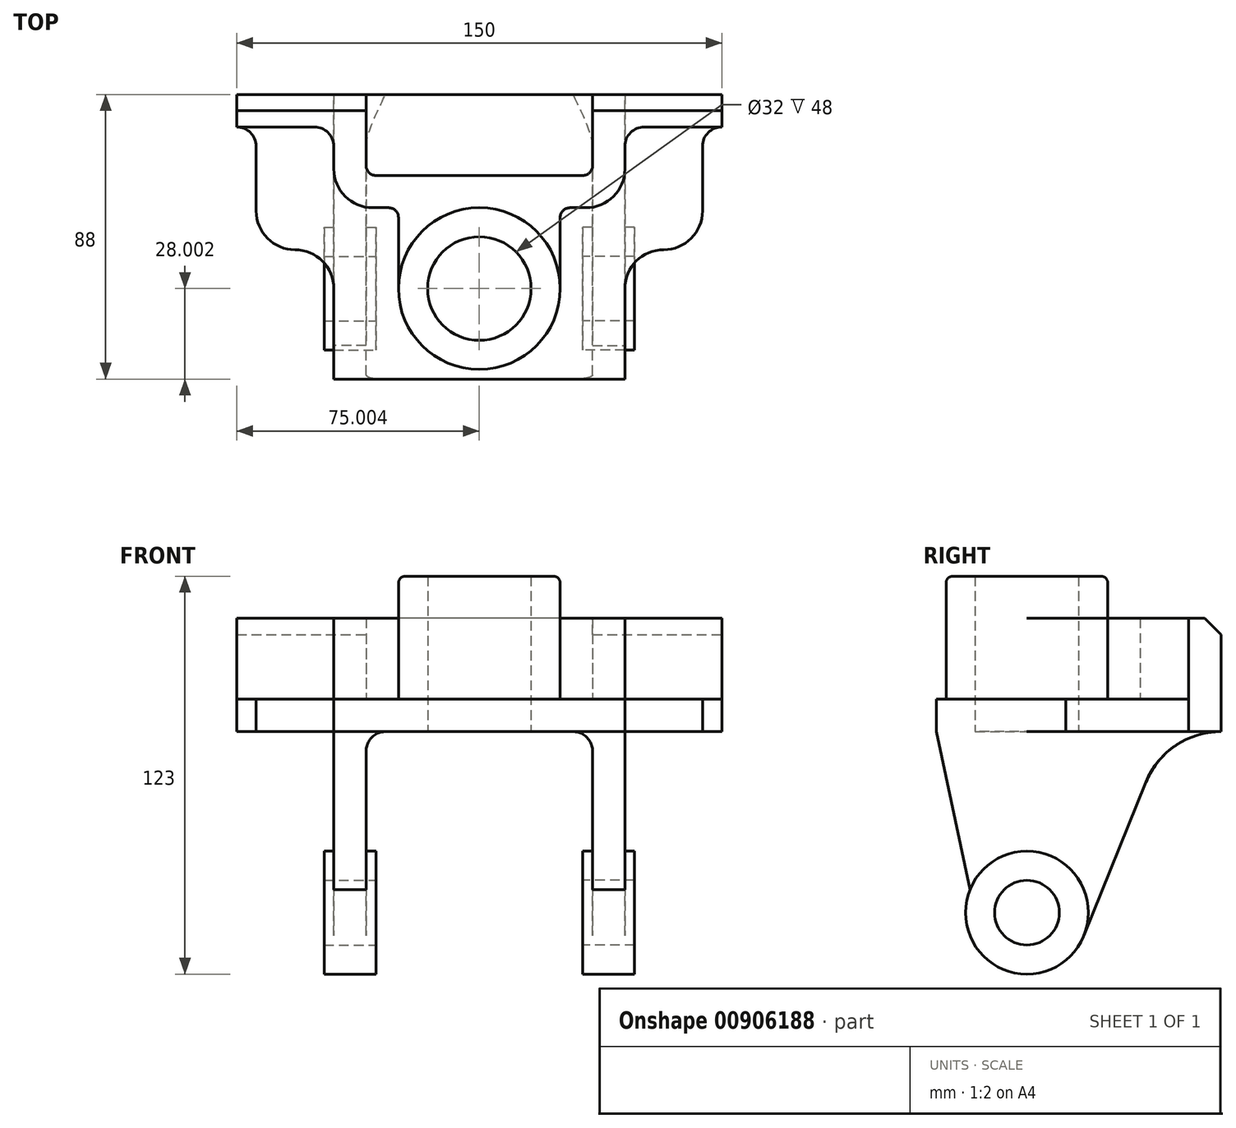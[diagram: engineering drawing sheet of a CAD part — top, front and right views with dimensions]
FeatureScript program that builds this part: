
annotation { "Feature Type Name" : "Feature", "Feature Type Description" : "" }
export const myFeature = defineFeature(function(context is Context, id is Id, definition is map)
    precondition{}
    {
        {
            var Q0;
            Q0=qCreatedBy(makeId("Top.planeOp"),FACE);
            var sketch = newSketch(context, id + "F0", { "sketchPlane" : qUnion([Q0])});
            skLineSegment(sketch, "E0.top", {"start": v(-82.05, 47.38) * mm, "end": v(67.95, 47.38) * mm});
            skLineSegment(sketch, "E0.left", {"start": v(-82.05, 37.38) * mm, "end": v(-82.05, 47.38) * mm});
            skLineSegment(sketch, "E0.right", {"start": v(67.95, 37.38) * mm, "end": v(67.95, 47.38) * mm});
            skLineSegment(sketch, "E1.0", {"start": v(61.95, 11.38) * mm, "end": v(61.95, 31.38) * mm});
            skLineSegment(sketch, "E2.0", {"start": v(-76.05, 11.38) * mm, "end": v(-76.05, 31.38) * mm});
            skArc(sketch, "E3.filletArc", {"start": v(67.95, 37.38) * mm, "mid": v(63.71, 35.62) * mm, "end": v(61.95, 31.38) * mm});
            skArc(sketch, "E4.filletArc", {"start": v(-76.05, 31.38) * mm, "mid": v(-77.8, 35.62) * mm, "end": v(-82.05, 37.38) * mm});
            skLineSegment(sketch, "E5.0", {"start": v(37.95, -12.62) * mm, "end": v(37.95, -40.62) * mm});
            skLineSegment(sketch, "E6.0", {"start": v(49.95, -0.62) * mm, "end": v(49.95, -0.62) * mm});
            skArc(sketch, "E7.filletArc", {"start": v(49.95, -0.62) * mm, "mid": v(41.47, -4.13) * mm, "end": v(37.95, -12.62) * mm});
            skArc(sketch, "E8.filletArc", {"start": v(49.95, -0.62) * mm, "mid": v(58.44, 2.9) * mm, "end": v(61.95, 11.38) * mm});
            skLineSegment(sketch, "E9", {"start": v(-7.05, 47.38) * mm, "end": v(-7.05, -47.77) * mm, "construction": true});
            skArc(sketch, "E10.MirrorCS", {"start": v(-64.05, -0.62) * mm, "mid": v(-72.53, 2.9) * mm, "end": v(-76.05, 11.38) * mm});
            skArc(sketch, "E11.MirrorCS", {"start": v(-64.05, -0.62) * mm, "mid": v(-55.56, -4.13) * mm, "end": v(-52.05, -12.62) * mm});
            skLineSegment(sketch, "E12", {"start": v(-52.05, -12.62) * mm, "end": v(-52.05, -40.62) * mm});
            skLineSegment(sketch, "E13", {"start": v(67.95, 37.38) * mm, "end": v(43.95, 37.38) * mm});
            skLineSegment(sketch, "E14", {"start": v(27.95, 47.38) * mm, "end": v(27.95, 25.38) * mm});
            skLineSegment(sketch, "E15.0", {"start": v(37.95, 31.38) * mm, "end": v(37.95, 24.38) * mm});
            skLineSegment(sketch, "E16", {"start": v(-52.05, -40.62) * mm, "end": v(37.95, -40.62) * mm});
            skArc(sketch, "E17.filletArc", {"start": v(43.95, 37.38) * mm, "mid": v(39.71, 35.62) * mm, "end": v(37.95, 31.38) * mm});
            skLineSegment(sketch, "E18.0", {"start": v(25.95, 12.38) * mm, "end": v(20.95, 12.38) * mm});
            skPoint(sketch, "E19.visualSharp", {"position": v(37.95, 12.38) * mm});
            skLineSegment(sketch, "E20.trimOffspring", {"start": v(24.95, 22.38) * mm, "end": v(-39.05, 22.38) * mm});
            skArc(sketch, "E21.filletArc", {"start": v(25.95, 12.38) * mm, "mid": v(34.44, 15.9) * mm, "end": v(37.95, 24.38) * mm});
            skCircle(sketch, "E22", {"center": v(-7.05, -12.62) * mm, "radius": 16 * mm});
            skCircle(sketch, "E23", {"center": v(-7.05, -12.62) * mm, "radius": 25 * mm});
            skLineSegment(sketch, "E24", {"start": v(17.95, -12.62) * mm, "end": v(17.95, 9.38) * mm});
            skArc(sketch, "E25.filletArc", {"start": v(20.95, 12.38) * mm, "mid": v(18.83, 11.5) * mm, "end": v(17.95, 9.38) * mm});
            skLineSegment(sketch, "E26.MirrorCS", {"start": v(-82.05, 37.38) * mm, "end": v(-58.05, 37.38) * mm});
            skArc(sketch, "E27.MirrorCS", {"start": v(-58.05, 37.38) * mm, "mid": v(-53.8, 35.62) * mm, "end": v(-52.05, 31.38) * mm});
            skLineSegment(sketch, "E28.MirrorCS", {"start": v(-52.05, 31.38) * mm, "end": v(-52.05, 24.38) * mm});
            skLineSegment(sketch, "E29.MirrorCS", {"start": v(-32.05, -12.62) * mm, "end": v(-32.05, 9.38) * mm});
            skArc(sketch, "E30.MirrorCS", {"start": v(-35.05, 12.38) * mm, "mid": v(-32.93, 11.5) * mm, "end": v(-32.05, 9.38) * mm});
            skArc(sketch, "E31.MirrorCS", {"start": v(-40.05, 12.38) * mm, "mid": v(-48.53, 15.9) * mm, "end": v(-52.05, 24.38) * mm});
            skLineSegment(sketch, "E32.MirrorCS", {"start": v(-40.05, 12.38) * mm, "end": v(-35.05, 12.38) * mm});
            skLineSegment(sketch, "E33.MirrorCS", {"start": v(-42.05, 47.38) * mm, "end": v(-42.05, 25.38) * mm});
            skArc(sketch, "E34.filletArc", {"start": v(24.95, 22.38) * mm, "mid": v(27.07, 23.26) * mm, "end": v(27.95, 25.38) * mm});
            skArc(sketch, "E35.filletArc", {"start": v(-42.05, 25.38) * mm, "mid": v(-41.17, 23.26) * mm, "end": v(-39.05, 22.38) * mm});
            skSolve(sketch);
        }
        {
            var Q0;
            Q0 = qSketchRegion(id + "F0", true);
            var Q1;
            Q1=makeQuery(id+"F0.imprint","IMPRINT",FACE,{"disambiguationData":[TD([[makeQuery(id+"F0.imprint","IMPRINT",EDGE,{"derivedFrom":sQuery(id+"F0.wireOp",EDGE,"E22")}),-1.0]])]});
            extrude(context, id + "F1", {"entities" : qUnion([Q0, Q1]), "depth" : 10 * mm, "offsetDistance" : 25 * mm});
        }
        {
            var Q0;
            {var subQ5=sQuery(id+"F0.wireOp",EDGE,"E0.left");Q0=makeQuery(id+"F0.imprint","IMPRINT",FACE,{"disambiguationData":[TD([[makeQuery(id+"F0.imprint","IMPRINT",EDGE,{"derivedFrom":subQ5}),-1.0]])]});}
            var Q1;
            Q1=makeQuery(id+"F0.imprint","IMPRINT",FACE,{"disambiguationData":[TD([[makeQuery(id+"F0.imprint","IMPRINT",EDGE,{"derivedFrom":sQuery(id+"F0.wireOp",EDGE,"E22")}),-1.0]])]});
            extrude(context, id + "F2", {"entities" : qUnion([Q0, Q1]), "operationType" : NewBodyOperationType.ADD, "depth" : 35 * mm, "offsetDistance" : 25 * mm});
        }
        {
            var Q0;
            Q0=makeQuery(id+"F0.imprint","IMPRINT",FACE,{"disambiguationData":[TD([[makeQuery(id+"F0.imprint","IMPRINT",EDGE,{"derivedFrom":sQuery(id+"F0.wireOp",EDGE,"E22")}),-1.0]])]});
            extrude(context, id + "F3", {"entities" : qUnion([Q0]), "operationType" : NewBodyOperationType.ADD, "depth" : 48 * mm, "offsetDistance" : 25 * mm});
        }
        {
            var Q0;
            Q0=makeQuery(id+"F1.opExtrude","SWEPT_FACE",FACE,{"disambiguationData":[OSD([sQuery(id+"F0.wireOp",EDGE,"E5.0")])]});
            var sketch = newSketch(context, id + "F4", { "sketchPlane" : qUnion([Q0])});
            skLineSegment(sketch, "E36", {"start": v(-12.62, 10) * mm, "end": v(-12.62, -56) * mm, "construction": true});
            skCircle(sketch, "E37", {"center": v(-12.62, -56) * mm, "radius": 10 * mm});
            skCircle(sketch, "E38", {"center": v(-12.62, -56) * mm, "radius": 19 * mm});
            skLineSegment(sketch, "E39", {"start": v(-40.62, 0) * mm, "end": v(-30.23, -48.88) * mm});
            skPoint(sketch, "E40.visualSharp", {"position": v(15.38, 0) * mm});
            skLineSegment(sketch, "E41", {"start": v(36.77, 0) * mm, "end": v(-40.62, 0) * mm});
            skLineSegment(sketch, "E42", {"start": v(-40.62, 0) * mm, "end": v(47.38, 0) * mm});
            skArc(sketch, "E43", {"start": v(47.38, 0) * mm, "mid": v(33.4, -4.27) * mm, "end": v(24.2, -15.63) * mm});
            skLineSegment(sketch, "E44", {"start": v(24.2, -15.63) * mm, "end": v(5, -63.12) * mm});
            skLineSegment(sketch, "E45", {"start": v(5, -63.12) * mm, "end": v(-30.23, -48.88) * mm});
            skSolve(sketch);
        }
        {
            var Q0;
            {var subQ2=sQuery(id+"F4.wireOp",EDGE,"E39");Q0=makeQuery(id+"F4.imprint","IMPRINT",FACE,{"disambiguationData":[TD([[makeQuery(id+"F4.imprint","IMPRINT",EDGE,{"derivedFrom":subQ2}),1.0]])]});}
            extrude(context, id + "F5", {"entities" : qUnion([Q0]), "operationType" : NewBodyOperationType.ADD, "oppositeDirection" : true, "depth" : 10 * mm, "offsetDistance" : 25 * mm});
        }
        {
            var Q0;
            Q0=makeQuery(id+"F4.imprint","IMPRINT",FACE,{"disambiguationData":[TD([[makeQuery(id+"F4.imprint","IMPRINT",EDGE,{"derivedFrom":sQuery(id+"F4.wireOp",EDGE,"E37")}),-1.0]])]});
            extrude(context, id + "F6", {"entities" : qUnion([Q0]), "operationType" : NewBodyOperationType.ADD, "depth" : 3 * mm, "offsetDistance" : 25 * mm, "hasSecondDirection" : true, "secondDirectionOppositeDirection" : true, "secondDirectionDepth" : 13 * mm});
        }
        {
            var Q0;
            Q0=makeQuery(id+"F5.opExtrude","CAP_EDGE",EDGE,{"disambiguationData":[OSD([sQuery(id+"F4.wireOp",EDGE,"E42")])],"isStart":false});
            fillet(context, id + "F7", {"entities" : qUnion([Q0]), "radius" : 6 * mm, "tangentPropagation" : true, "allowEdgeOverflow" : false});
        }
        {
            var Q0;
            Q0=makeQuery(id+"F1.opExtrude","CAP_EDGE",EDGE,{"disambiguationData":[OSD([sQuery(id+"F0.wireOp",EDGE,"E0.top")])],"isStart":false});
            cPoint(context, id + "F8", {"entities" : qUnion([Q0]), "parameter" : 0.5});
        }
        {
            var Q0;
            Q0=makeQuery(id+"F2.boolean.opBoolean","INTERSECT",EDGE,{"derivedFrom":[makeQuery(id+"F1.opExtrude","CAP_FACE",FACE,{"disambiguationData":[OSD([sQuery(id+"F0.wireOp",EDGE,"E0.top"),sQuery(id+"F0.wireOp",EDGE,"E0.left"),sQuery(id+"F0.wireOp",EDGE,"E0.right"),sQuery(id+"F0.wireOp",EDGE,"E1.0"),sQuery(id+"F0.wireOp",EDGE,"E2.0"),sQuery(id+"F0.wireOp",EDGE,"E3.filletArc"),sQuery(id+"F0.wireOp",EDGE,"E4.filletArc"),sQuery(id+"F0.wireOp",EDGE,"E5.0"),sQuery(id+"F0.wireOp",EDGE,"E7.filletArc"),sQuery(id+"F0.wireOp",EDGE,"E8.filletArc"),sQuery(id+"F0.wireOp",EDGE,"E10.MirrorCS"),sQuery(id+"F0.wireOp",EDGE,"E11.MirrorCS"),sQuery(id+"F0.wireOp",EDGE,"E12"),sQuery(id+"F0.wireOp",EDGE,"E16"),sQuery(id+"F0.wireOp",EDGE,"E22")])],"isStart":false}),makeQuery(id+"F2.opExtrude","SWEPT_FACE",FACE,{"disambiguationData":[OSD([sQuery(id+"F0.wireOp",EDGE,"E20.trimOffspring")])]})]});
            cPoint(context, id + "F9", {"entities" : qUnion([Q0]), "parameter" : 0.5});
        }
        {
            var Q0;
            Q0=makeQuery(id+"F2.opExtrude","CAP_EDGE",EDGE,{"disambiguationData":[OSD([sQuery(id+"F0.wireOp",EDGE,"E20.trimOffspring")])],"isStart":false});
            cPoint(context, id + "F10", {"entities" : qUnion([Q0]), "parameter" : 0.5});
        }
        {
            var Q0;
            Q0 = qCreatedBy(id + "F8" ,VERTEX);
            var Q1;
            Q1 = qCreatedBy(id + "F9" ,VERTEX);
            var Q2;
            Q2 = qCreatedBy(id + "F10" ,VERTEX);
            cPlane(context, id + "F11", {"entities" : qUnion([Q0, Q1, Q2]), "cplaneType" : CPlaneType.THREE_POINT, "offset" : 25 * mm, "oppositeDirection" : true, "width" : 150 * mm, "height" : 150 * mm});
        }
        {
            var Q0;
            Q0=makeQuery(id+"F1.opExtrude","SWEPT_BODY",BODY,{"disambiguationData":[OSD([sQuery(id+"F0.wireOp",EDGE,"E0.top"),sQuery(id+"F0.wireOp",EDGE,"E0.left"),sQuery(id+"F0.wireOp",EDGE,"E0.right"),sQuery(id+"F0.wireOp",EDGE,"E1.0"),sQuery(id+"F0.wireOp",EDGE,"E2.0"),sQuery(id+"F0.wireOp",EDGE,"E3.filletArc"),sQuery(id+"F0.wireOp",EDGE,"E4.filletArc"),sQuery(id+"F0.wireOp",EDGE,"E5.0"),sQuery(id+"F0.wireOp",EDGE,"E7.filletArc"),sQuery(id+"F0.wireOp",EDGE,"E8.filletArc"),sQuery(id+"F0.wireOp",EDGE,"E10.MirrorCS"),sQuery(id+"F0.wireOp",EDGE,"E11.MirrorCS"),sQuery(id+"F0.wireOp",EDGE,"E12"),sQuery(id+"F0.wireOp",EDGE,"E16"),sQuery(id+"F0.wireOp",EDGE,"E22")])]});
            var Q1;
            Q1=qCreatedBy(id+"F11.planeOp",FACE);
            mirror(context, id + "F12", {"operationType" : NewBodyOperationType.ADD, "entities" : qUnion([Q0]), "mirrorPlane" : qUnion([Q1])});
        }
        {
            var Q0;
            Q0=makeQuery(id+"F3.opExtrude","CAP_EDGE",EDGE,{"disambiguationData":[OSD([sQuery(id+"F0.wireOp",EDGE,"E23")])],"isStart":false});
            fillet(context, id + "F13", {"entities" : qUnion([Q0]), "radius" : 2 * mm, "tangentPropagation" : true, "allowEdgeOverflow" : false});
        }
        {
            var Q0;
            {var subQ0=sQuery(id+"F0.wireOp",EDGE,"E0.top");Q0=makeQuery(id+"F2.opExtrude","CAP_EDGE",EDGE,{"disambiguationData":[OSD([subQ0]),TDD([makeQuery(id+"F0.imprint","IMPRINT",EDGE,{"disambiguationData":[TD([[makeQuery(id+"F0.imprint","INTERSECT",VERTEX,{"derivedFrom":[subQ0,sQuery(id+"F0.wireOp",EDGE,"E0.right")]}),1.0]])],"derivedFrom":subQ0})])],"isStart":false});}
            var Q1;
            {var subQ0=sQuery(id+"F0.wireOp",EDGE,"E0.top");Q1=makeQuery(id+"F2.opExtrude","CAP_EDGE",EDGE,{"disambiguationData":[OSD([subQ0]),TDD([makeQuery(id+"F0.imprint","IMPRINT",EDGE,{"disambiguationData":[TD([[makeQuery(id+"F0.imprint","INTERSECT",VERTEX,{"derivedFrom":[subQ0,sQuery(id+"F0.wireOp",EDGE,"E0.left")]}),-1.0]])],"derivedFrom":subQ0})])],"isStart":false});}
            chamfer(context, id + "F14", {"entities" : qUnion([Q0, Q1]), "width" : 5 * mm, "tangentPropagation" : true});
        }
    });
